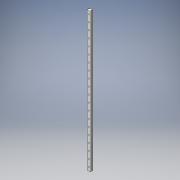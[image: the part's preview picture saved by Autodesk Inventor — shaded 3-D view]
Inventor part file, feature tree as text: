
AUTODESK INVENTOR PART (.ipt)
format: ipt  version: 2017.3 (Build 213256000, 256)  size: 195,584 bytes
history: mixed  units: mm
features: thicken_offset x2, extrude x2, pattern_linear x2, sketch x2, other x1, imported_body x1
ambient origin geometry x8: Origin, YZ Plane, XZ Plane, XY Plane, X Axis, Y Axis, Z Axis, Center Point
bodies: Solid1 (imported_parasolid)
feature tree (10):
  thicken_offset  "Thicken1"
  extrude  "Extrusion1"  Depth=145.0mm
  pattern_linear  "Rectangular Pattern1"  Spacing1=4.5mm  [1 undecoded]
  extrude  "Extrusion2"  Depth=10.0mm TaperAngle=0.0deg
  pattern_linear  "Rectangular Pattern2"  Count1=7  [1 undecoded]
  thicken_offset  "Thicken2"
  sketch  "Sketch1"  dims[d0=145.0mm d1=150.0mm d2=20.0mm]
  sketch  "Sketch2"  dims[d3=3.5mm d4=4.5mm d5=10.0mm d6=0.0mm d7=70.0mm d9=20.0mm d10=6.0mm d11=3.5mm d12=0.0mm d13=70.0mm d15=20.0mm d16=5.0mm d17=5.0mm]
  other  "LPattern1"
  imported_body  NMx_Import_Brep_tag  [imported B-rep: ~78 faces, bbox_mm=[9.0, 6.5, 400.0]]
note: 2 required parameter values undecoded (feature->parameter linkage not recoverable at this tier; creation-order binding heuristic only, values carry confidence <= 0.55)
